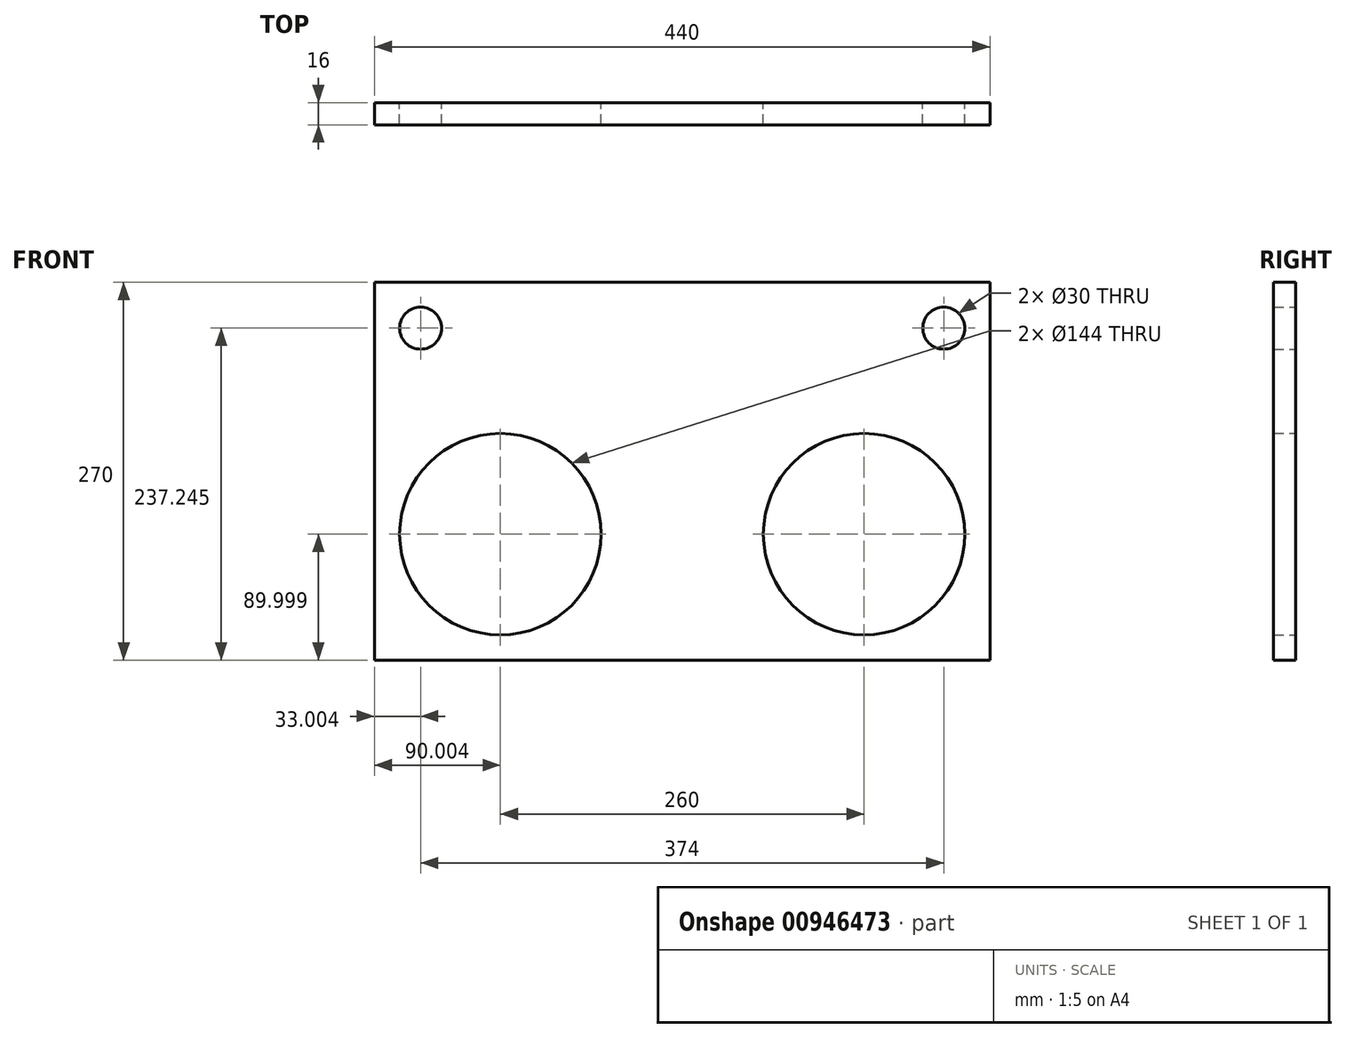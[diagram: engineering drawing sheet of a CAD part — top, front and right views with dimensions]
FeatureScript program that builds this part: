
annotation { "Feature Type Name" : "Feature", "Feature Type Description" : "" }
export const myFeature = defineFeature(function(context is Context, id is Id, definition is map)
    precondition{}
    {
        {
            var Q0;
            Q0=qCreatedBy(makeId("Front.planeOp"),FACE);
            var sketch = newSketch(context, id + "F0", { "sketchPlane" : qUnion([Q0])});
            skLineSegment(sketch, "E0.bottom", {"start": v(221.63, 90.04) * mm, "end": v(-218.37, 90.04) * mm});
            skLineSegment(sketch, "E0.top", {"start": v(221.63, -179.96) * mm, "end": v(-218.37, -179.96) * mm});
            skLineSegment(sketch, "E0.left", {"start": v(221.63, 90.04) * mm, "end": v(221.63, -179.96) * mm});
            skLineSegment(sketch, "E0.right", {"start": v(-218.37, 90.04) * mm, "end": v(-218.37, -179.96) * mm});
            skCircle(sketch, "E1", {"center": v(-128.37, -89.96) * mm, "radius": 72 * mm});
            skCircle(sketch, "E2.MirrorC", {"center": v(131.63, -89.96) * mm, "radius": 72 * mm});
            skCircle(sketch, "E3", {"center": v(-185.37, 57.29) * mm, "radius": 15 * mm});
            skCircle(sketch, "E4.MirrorC", {"center": v(188.63, 57.29) * mm, "radius": 15 * mm});
            skPoint(sketch, "E5.end.orphan", {"position": v(1.63, 90.04) * mm});
            skPoint(sketch, "E5.start.orphan", {"position": v(1.63, -179.96) * mm});
            skSolve(sketch);
        }
        {
            var Q0;
            Q0 = qSketchRegion(id + "F0", true);
            extrude(context, id + "F1", {"entities" : qUnion([Q0]), "depth" : 16 * mm, "offsetDistance" : 25 * mm});
        }
    });
